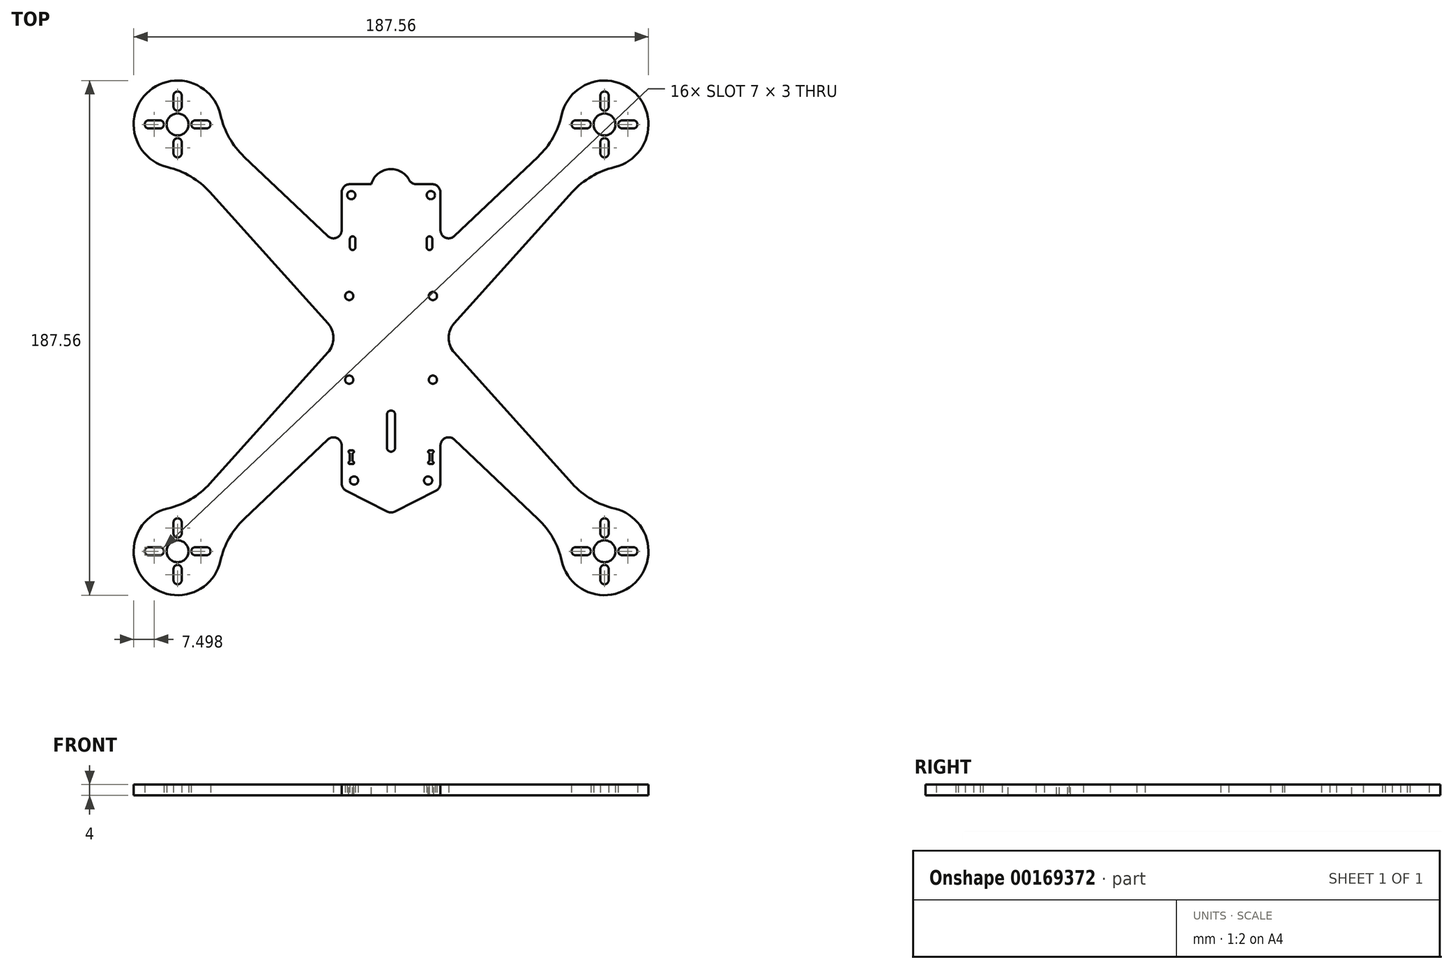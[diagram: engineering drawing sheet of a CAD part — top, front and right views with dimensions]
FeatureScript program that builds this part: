
annotation { "Feature Type Name" : "Feature", "Feature Type Description" : "" }
export const myFeature = defineFeature(function(context is Context, id is Id, definition is map)
    precondition{}
    {
        {
            var Q0;
            Q0=qCreatedBy(makeId("Top.planeOp"),FACE);
            var sketch = newSketch(context, id + "F0", { "sketchPlane" : qUnion([Q0])});
            skLineSegment(sketch, "E0.bottom", {"start": v(-15, 56) * mm, "end": v(15, 56) * mm});
            skLineSegment(sketch, "E0.left", {"start": v(-18, 53) * mm, "end": v(-18, 39.26) * mm});
            skLineSegment(sketch, "E0.right", {"start": v(18, 53) * mm, "end": v(18, 39.26) * mm});
            skCircle(sketch, "E1", {"center": v(0, 0) * mm, "radius": 110 * mm, "construction": true});
            skLineSegment(sketch, "E2", {"start": v(0, 0) * mm, "end": v(-77.78, 77.78) * mm, "construction": true});
            skLineSegment(sketch, "E3", {"start": v(0, 0) * mm, "end": v(-77.78, -77.78) * mm, "construction": true});
            skLineSegment(sketch, "E4", {"start": v(0, 0) * mm, "end": v(77.78, 77.78) * mm, "construction": true});
            skLineSegment(sketch, "E5", {"start": v(0, 0) * mm, "end": v(77.78, -77.78) * mm, "construction": true});
            skCircle(sketch, "E6", {"center": v(-77.78, 77.78) * mm, "radius": 63.5 * mm, "construction": true});
            skCircle(sketch, "E7", {"center": v(-77.78, -77.78) * mm, "radius": 63.5 * mm, "construction": true});
            skCircle(sketch, "E8", {"center": v(77.78, -77.78) * mm, "radius": 63.5 * mm, "construction": true});
            skCircle(sketch, "E9", {"center": v(77.78, 77.78) * mm, "radius": 63.5 * mm, "construction": true});
            skLineSegment(sketch, "E10.trimOffspring", {"start": v(-18, -39.26) * mm, "end": v(-18, -53) * mm});
            skLineSegment(sketch, "E11.trimOffspring", {"start": v(18, -39.26) * mm, "end": v(18, -53) * mm});
            skCircle(sketch, "E12", {"center": v(-15.25, 15.25) * mm, "radius": 1.5 * mm});
            skCircle(sketch, "E13.0.1.0", {"center": v(-15.25, -15.25) * mm, "radius": 1.5 * mm});
            skCircle(sketch, "E13.1.0.0", {"center": v(15.25, 15.25) * mm, "radius": 1.5 * mm});
            skCircle(sketch, "E13.1.1.0", {"center": v(15.25, -15.25) * mm, "radius": 1.5 * mm});
            skLineSegment(sketch, "E13.direction1", {"start": v(-15.25, 15.25) * mm, "end": v(15.25, 15.25) * mm, "construction": true});
            skLineSegment(sketch, "E13.direction2", {"start": v(-15.25, 15.25) * mm, "end": v(-15.25, -15.25) * mm, "construction": true});
            skPoint(sketch, "E14.visualSharp", {"position": v(-18, -32.28) * mm});
            skPoint(sketch, "E15.visualSharp", {"position": v(18, -32.28) * mm});
            skPoint(sketch, "E16.visualSharp", {"position": v(18, 32.28) * mm});
            skPoint(sketch, "E17.visualSharp", {"position": v(-18, 32.28) * mm});
            skCircle(sketch, "E18", {"center": v(-13.5, -52) * mm, "radius": 1.5 * mm});
            skCircle(sketch, "E19", {"center": v(-14.5, 52) * mm, "radius": 1.5 * mm});
            skCircle(sketch, "E20.1.0.0", {"center": v(14.5, 52) * mm, "radius": 1.5 * mm});
            skLineSegment(sketch, "E21", {"start": v(-14.5, 52) * mm, "end": v(14.5, 52) * mm, "construction": true});
            skCircle(sketch, "E22.1.0.0", {"center": v(13.5, -52) * mm, "radius": 1.5 * mm});
            skLineSegment(sketch, "E22.direction1", {"start": v(-13.5, -52) * mm, "end": v(13.5, -52) * mm, "construction": true});
            skPoint(sketch, "E23.visualSharp", {"position": v(-18, 56) * mm});
            skArc(sketch, "E23.filletArc", {"start": v(-15, 56) * mm, "mid": v(-17.12, 55.12) * mm, "end": v(-18, 53) * mm});
            skPoint(sketch, "E24.visualSharp", {"position": v(18, 56) * mm});
            skArc(sketch, "E24.filletArc", {"start": v(18, 53) * mm, "mid": v(17.12, 55.12) * mm, "end": v(15, 56) * mm});
            skArc(sketch, "E25", {"start": v(-81.44, -62.2) * mm, "mid": v(-89.03, -89.16) * mm, "end": v(-62.16, -81.25) * mm});
            skArc(sketch, "E26", {"start": v(62.16, -81.25) * mm, "mid": v(89.03, -89.16) * mm, "end": v(81.44, -62.2) * mm});
            skArc(sketch, "E27", {"start": v(81.44, 62.2) * mm, "mid": v(89.03, 89.16) * mm, "end": v(62.16, 81.25) * mm});
            skArc(sketch, "E28", {"start": v(-62.16, 81.25) * mm, "mid": v(-89.03, 89.16) * mm, "end": v(-81.44, 62.2) * mm});
            skLineSegment(sketch, "E29", {"start": v(-23.03, 5.35) * mm, "end": v(-66, 53.07) * mm});
            skLineSegment(sketch, "E30", {"start": v(-23.07, 37.08) * mm, "end": v(-53.53, 65.99) * mm});
            skPoint(sketch, "E31.visualSharp", {"position": v(-62.19, 74.2) * mm});
            skArc(sketch, "E31.filletArc", {"start": v(-62.16, 81.25) * mm, "mid": v(-58.98, 72.97) * mm, "end": v(-53.53, 65.99) * mm});
            skPoint(sketch, "E32.visualSharp", {"position": v(-74.2, 62.19) * mm});
            skArc(sketch, "E32.filletArc", {"start": v(-66, 53.07) * mm, "mid": v(-73.02, 58.82) * mm, "end": v(-81.44, 62.2) * mm});
            skLineSegment(sketch, "E33", {"start": v(23.07, 37.08) * mm, "end": v(53.53, 65.99) * mm});
            skLineSegment(sketch, "E34", {"start": v(23.03, 5.35) * mm, "end": v(66, 53.07) * mm});
            skPoint(sketch, "E35.visualSharp", {"position": v(62.19, 74.2) * mm});
            skArc(sketch, "E35.filletArc", {"start": v(53.53, 65.99) * mm, "mid": v(58.98, 72.97) * mm, "end": v(62.16, 81.25) * mm});
            skPoint(sketch, "E36.visualSharp", {"position": v(74.2, 62.19) * mm});
            skArc(sketch, "E36.filletArc", {"start": v(81.44, 62.2) * mm, "mid": v(73.02, 58.82) * mm, "end": v(66, 53.07) * mm});
            skLineSegment(sketch, "E37", {"start": v(-23.03, -5.35) * mm, "end": v(-66, -53.07) * mm});
            skLineSegment(sketch, "E38", {"start": v(-53.53, -65.99) * mm, "end": v(-23.07, -37.08) * mm});
            skLineSegment(sketch, "E39", {"start": v(23.07, -37.08) * mm, "end": v(53.53, -65.99) * mm});
            skLineSegment(sketch, "E40", {"start": v(66, -53.07) * mm, "end": v(23.03, -5.35) * mm});
            skPoint(sketch, "E41.visualSharp", {"position": v(-74.2, -62.19) * mm});
            skArc(sketch, "E41.filletArc", {"start": v(-81.44, -62.2) * mm, "mid": v(-73.02, -58.82) * mm, "end": v(-66, -53.07) * mm});
            skPoint(sketch, "E42.visualSharp", {"position": v(-62.19, -74.2) * mm});
            skArc(sketch, "E42.filletArc", {"start": v(-53.53, -65.99) * mm, "mid": v(-58.98, -72.97) * mm, "end": v(-62.16, -81.25) * mm});
            skPoint(sketch, "E43.visualSharp", {"position": v(62.19, -74.2) * mm});
            skArc(sketch, "E43.filletArc", {"start": v(62.16, -81.25) * mm, "mid": v(58.98, -72.97) * mm, "end": v(53.53, -65.99) * mm});
            skPoint(sketch, "E44.visualSharp", {"position": v(74.2, -62.19) * mm});
            skArc(sketch, "E44.filletArc", {"start": v(66, -53.07) * mm, "mid": v(73.02, -58.82) * mm, "end": v(81.44, -62.2) * mm});
            skCircle(sketch, "E45", {"center": v(-77.78, 77.78) * mm, "radius": 4 * mm});
            skCircle(sketch, "E46", {"center": v(77.78, 77.78) * mm, "radius": 4 * mm});
            skCircle(sketch, "E47", {"center": v(77.78, -77.78) * mm, "radius": 4 * mm});
            skCircle(sketch, "E48", {"center": v(-77.78, -77.78) * mm, "radius": 4 * mm});
            skArc(sketch, "E49", {"start": v(1.5, -28) * mm, "mid": v(0, -26.5) * mm, "end": v(-1.5, -28) * mm});
            skArc(sketch, "E50", {"start": v(-1.5, -40) * mm, "mid": v(0, -41.5) * mm, "end": v(1.5, -40) * mm});
            skLineSegment(sketch, "E51", {"start": v(-1.5, -28) * mm, "end": v(-1.5, -40) * mm});
            skLineSegment(sketch, "E52", {"start": v(1.5, -28) * mm, "end": v(1.5, -40) * mm});
            skArc(sketch, "E53.filletArc", {"start": v(-18, -39.26) * mm, "mid": v(-19.82, -36.5) * mm, "end": v(-23.07, -37.08) * mm});
            skArc(sketch, "E54.filletArc", {"start": v(23.07, -37.08) * mm, "mid": v(19.82, -36.5) * mm, "end": v(18, -39.26) * mm});
            skArc(sketch, "E55.filletArc", {"start": v(-23.07, 37.08) * mm, "mid": v(-19.82, 36.5) * mm, "end": v(-18, 39.26) * mm});
            skArc(sketch, "E56.filletArc", {"start": v(18, 39.26) * mm, "mid": v(19.82, 36.5) * mm, "end": v(23.07, 37.08) * mm});
            skArc(sketch, "E57", {"start": v(-13, 36) * mm, "mid": v(-14, 37) * mm, "end": v(-15, 36) * mm});
            skArc(sketch, "E58", {"start": v(-15, 33) * mm, "mid": v(-14, 32) * mm, "end": v(-13, 33) * mm});
            skLineSegment(sketch, "E59", {"start": v(-14, 36) * mm, "end": v(-14, 33) * mm, "construction": true});
            skLineSegment(sketch, "E60", {"start": v(-15, 36) * mm, "end": v(-15, 33) * mm});
            skLineSegment(sketch, "E61", {"start": v(-13, 36) * mm, "end": v(-13, 33) * mm});
            skLineSegment(sketch, "E62.MirrorCS", {"start": v(14, 36) * mm, "end": v(14, 33) * mm, "construction": true});
            skArc(sketch, "E63.MirrorCS", {"start": v(13, 36) * mm, "mid": v(14, 37) * mm, "end": v(15, 36) * mm});
            skArc(sketch, "E64.MirrorCS", {"start": v(15, 33) * mm, "mid": v(14, 32) * mm, "end": v(13, 33) * mm});
            skLineSegment(sketch, "E65.MirrorCS", {"start": v(13, 36) * mm, "end": v(13, 33) * mm});
            skLineSegment(sketch, "E66.MirrorCS", {"start": v(15, 36) * mm, "end": v(15, 33) * mm});
            skArc(sketch, "E67.filletArc", {"start": v(-23.03, -5.35) * mm, "mid": v(-20.98, 0) * mm, "end": v(-23.03, 5.35) * mm});
            skArc(sketch, "E68.filletArc", {"start": v(23.03, 5.35) * mm, "mid": v(20.98, 0) * mm, "end": v(23.03, -5.35) * mm});
            skLineSegment(sketch, "E69", {"start": v(-15, -56) * mm, "end": v(15, -56) * mm});
            skPoint(sketch, "E70.visualSharp", {"position": v(-18, -56) * mm});
            skArc(sketch, "E70.filletArc", {"start": v(-18, -53) * mm, "mid": v(-17.12, -55.12) * mm, "end": v(-15, -56) * mm});
            skPoint(sketch, "E71.visualSharp", {"position": v(18, -56) * mm});
            skArc(sketch, "E71.filletArc", {"start": v(15, -56) * mm, "mid": v(17.12, -55.12) * mm, "end": v(18, -53) * mm});
            skLineSegment(sketch, "E72", {"start": v(-77.78, 77.78) * mm, "end": v(-89.03, 89.16) * mm, "construction": true});
            skLineSegment(sketch, "E73", {"start": v(-77.78, 77.78) * mm, "end": v(-89.1, 66.47) * mm, "construction": true});
            skLineSegment(sketch, "E74", {"start": v(-77.78, 77.78) * mm, "end": v(-66.47, 89.1) * mm, "construction": true});
            skArc(sketch, "E75", {"start": v(-79.28, 84.28) * mm, "mid": v(-77.78, 82.78) * mm, "end": v(-76.28, 84.28) * mm});
            skArc(sketch, "E76", {"start": v(-76.28, 88.28) * mm, "mid": v(-77.78, 89.78) * mm, "end": v(-79.28, 88.28) * mm});
            skLineSegment(sketch, "E77", {"start": v(-79.28, 88.28) * mm, "end": v(-79.28, 84.28) * mm});
            skLineSegment(sketch, "E78", {"start": v(-76.28, 88.28) * mm, "end": v(-76.28, 84.28) * mm});
            skLineSegment(sketch, "E79", {"start": v(-77.78, 77.78) * mm, "end": v(-77.78, 93.78) * mm, "construction": true});
            skArc(sketch, "E80.1.0", {"start": v(-88.28, 79.28) * mm, "mid": v(-89.78, 77.78) * mm, "end": v(-88.28, 76.28) * mm});
            skArc(sketch, "E80.1.1", {"start": v(-84.28, 76.28) * mm, "mid": v(-82.78, 77.78) * mm, "end": v(-84.28, 79.28) * mm});
            skLineSegment(sketch, "E80.1.2", {"start": v(-88.28, 79.28) * mm, "end": v(-84.28, 79.28) * mm});
            skLineSegment(sketch, "E80.1.3", {"start": v(-88.28, 76.28) * mm, "end": v(-84.28, 76.28) * mm});
            skArc(sketch, "E80.2.0", {"start": v(-79.28, 67.28) * mm, "mid": v(-77.78, 65.78) * mm, "end": v(-76.28, 67.28) * mm});
            skArc(sketch, "E80.2.1", {"start": v(-76.28, 71.28) * mm, "mid": v(-77.78, 72.78) * mm, "end": v(-79.28, 71.28) * mm});
            skLineSegment(sketch, "E80.2.2", {"start": v(-79.28, 67.28) * mm, "end": v(-79.28, 71.28) * mm});
            skLineSegment(sketch, "E80.2.3", {"start": v(-76.28, 67.28) * mm, "end": v(-76.28, 71.28) * mm});
            skArc(sketch, "E80.3.0", {"start": v(-67.28, 76.28) * mm, "mid": v(-65.78, 77.78) * mm, "end": v(-67.28, 79.28) * mm});
            skArc(sketch, "E80.3.1", {"start": v(-71.28, 79.28) * mm, "mid": v(-72.78, 77.78) * mm, "end": v(-71.28, 76.28) * mm});
            skLineSegment(sketch, "E80.3.2", {"start": v(-67.28, 76.28) * mm, "end": v(-71.28, 76.28) * mm});
            skLineSegment(sketch, "E80.3.3", {"start": v(-67.28, 79.28) * mm, "end": v(-71.28, 79.28) * mm});
            skLineSegment(sketch, "E81.1.0", {"start": v(-88.28, -79.28) * mm, "end": v(-84.28, -79.28) * mm});
            skArc(sketch, "E81.1.1", {"start": v(-88.28, -76.28) * mm, "mid": v(-89.78, -77.78) * mm, "end": v(-88.28, -79.28) * mm});
            skLineSegment(sketch, "E81.1.2", {"start": v(-88.28, -76.28) * mm, "end": v(-84.28, -76.28) * mm});
            skArc(sketch, "E81.1.3", {"start": v(-84.28, -79.28) * mm, "mid": v(-82.78, -77.78) * mm, "end": v(-84.28, -76.28) * mm});
            skArc(sketch, "E81.1.4", {"start": v(-76.28, -67.28) * mm, "mid": v(-77.78, -65.78) * mm, "end": v(-79.28, -67.28) * mm});
            skLineSegment(sketch, "E81.1.5", {"start": v(-79.28, -67.28) * mm, "end": v(-79.28, -71.28) * mm});
            skLineSegment(sketch, "E81.1.6", {"start": v(-76.28, -67.28) * mm, "end": v(-76.28, -71.28) * mm});
            skArc(sketch, "E81.1.7", {"start": v(-79.28, -71.28) * mm, "mid": v(-77.78, -72.78) * mm, "end": v(-76.28, -71.28) * mm});
            skLineSegment(sketch, "E81.1.8", {"start": v(-67.28, -79.28) * mm, "end": v(-71.28, -79.28) * mm});
            skArc(sketch, "E81.1.9", {"start": v(-71.28, -76.28) * mm, "mid": v(-72.78, -77.78) * mm, "end": v(-71.28, -79.28) * mm});
            skLineSegment(sketch, "E81.1.10", {"start": v(-67.28, -76.28) * mm, "end": v(-71.28, -76.28) * mm});
            skArc(sketch, "E81.1.11", {"start": v(-67.28, -79.28) * mm, "mid": v(-65.78, -77.78) * mm, "end": v(-67.28, -76.28) * mm});
            skArc(sketch, "E81.1.12", {"start": v(-76.28, -84.28) * mm, "mid": v(-77.78, -82.78) * mm, "end": v(-79.28, -84.28) * mm});
            skLineSegment(sketch, "E81.1.13", {"start": v(-76.28, -88.28) * mm, "end": v(-76.28, -84.28) * mm});
            skLineSegment(sketch, "E81.1.14", {"start": v(-79.28, -88.28) * mm, "end": v(-79.28, -84.28) * mm});
            skArc(sketch, "E81.1.15", {"start": v(-79.28, -88.28) * mm, "mid": v(-77.78, -89.78) * mm, "end": v(-76.28, -88.28) * mm});
            skLineSegment(sketch, "E81.2.0", {"start": v(79.28, -88.28) * mm, "end": v(79.28, -84.28) * mm});
            skArc(sketch, "E81.2.1", {"start": v(76.28, -88.28) * mm, "mid": v(77.78, -89.78) * mm, "end": v(79.28, -88.28) * mm});
            skLineSegment(sketch, "E81.2.2", {"start": v(76.28, -88.28) * mm, "end": v(76.28, -84.28) * mm});
            skArc(sketch, "E81.2.3", {"start": v(79.28, -84.28) * mm, "mid": v(77.78, -82.78) * mm, "end": v(76.28, -84.28) * mm});
            skArc(sketch, "E81.2.4", {"start": v(67.28, -76.28) * mm, "mid": v(65.78, -77.78) * mm, "end": v(67.28, -79.28) * mm});
            skLineSegment(sketch, "E81.2.5", {"start": v(67.28, -79.28) * mm, "end": v(71.28, -79.28) * mm});
            skLineSegment(sketch, "E81.2.6", {"start": v(67.28, -76.28) * mm, "end": v(71.28, -76.28) * mm});
            skArc(sketch, "E81.2.7", {"start": v(71.28, -79.28) * mm, "mid": v(72.78, -77.78) * mm, "end": v(71.28, -76.28) * mm});
            skLineSegment(sketch, "E81.2.8", {"start": v(79.28, -67.28) * mm, "end": v(79.28, -71.28) * mm});
            skArc(sketch, "E81.2.9", {"start": v(76.28, -71.28) * mm, "mid": v(77.78, -72.78) * mm, "end": v(79.28, -71.28) * mm});
            skLineSegment(sketch, "E81.2.10", {"start": v(76.28, -67.28) * mm, "end": v(76.28, -71.28) * mm});
            skArc(sketch, "E81.2.11", {"start": v(79.28, -67.28) * mm, "mid": v(77.78, -65.78) * mm, "end": v(76.28, -67.28) * mm});
            skArc(sketch, "E81.2.12", {"start": v(84.28, -76.28) * mm, "mid": v(82.78, -77.78) * mm, "end": v(84.28, -79.28) * mm});
            skLineSegment(sketch, "E81.2.13", {"start": v(88.28, -76.28) * mm, "end": v(84.28, -76.28) * mm});
            skLineSegment(sketch, "E81.2.14", {"start": v(88.28, -79.28) * mm, "end": v(84.28, -79.28) * mm});
            skArc(sketch, "E81.2.15", {"start": v(88.28, -79.28) * mm, "mid": v(89.78, -77.78) * mm, "end": v(88.28, -76.28) * mm});
            skLineSegment(sketch, "E81.3.0", {"start": v(88.28, 79.28) * mm, "end": v(84.28, 79.28) * mm});
            skArc(sketch, "E81.3.1", {"start": v(88.28, 76.28) * mm, "mid": v(89.78, 77.78) * mm, "end": v(88.28, 79.28) * mm});
            skLineSegment(sketch, "E81.3.2", {"start": v(88.28, 76.28) * mm, "end": v(84.28, 76.28) * mm});
            skArc(sketch, "E81.3.3", {"start": v(84.28, 79.28) * mm, "mid": v(82.78, 77.78) * mm, "end": v(84.28, 76.28) * mm});
            skArc(sketch, "E81.3.4", {"start": v(76.28, 67.28) * mm, "mid": v(77.78, 65.78) * mm, "end": v(79.28, 67.28) * mm});
            skLineSegment(sketch, "E81.3.5", {"start": v(79.28, 67.28) * mm, "end": v(79.28, 71.28) * mm});
            skLineSegment(sketch, "E81.3.6", {"start": v(76.28, 67.28) * mm, "end": v(76.28, 71.28) * mm});
            skArc(sketch, "E81.3.7", {"start": v(79.28, 71.28) * mm, "mid": v(77.78, 72.78) * mm, "end": v(76.28, 71.28) * mm});
            skLineSegment(sketch, "E81.3.8", {"start": v(67.28, 79.28) * mm, "end": v(71.28, 79.28) * mm});
            skArc(sketch, "E81.3.9", {"start": v(71.28, 76.28) * mm, "mid": v(72.78, 77.78) * mm, "end": v(71.28, 79.28) * mm});
            skLineSegment(sketch, "E81.3.10", {"start": v(67.28, 76.28) * mm, "end": v(71.28, 76.28) * mm});
            skArc(sketch, "E81.3.11", {"start": v(67.28, 79.28) * mm, "mid": v(65.78, 77.78) * mm, "end": v(67.28, 76.28) * mm});
            skArc(sketch, "E81.3.12", {"start": v(76.28, 84.28) * mm, "mid": v(77.78, 82.78) * mm, "end": v(79.28, 84.28) * mm});
            skLineSegment(sketch, "E81.3.13", {"start": v(76.28, 88.28) * mm, "end": v(76.28, 84.28) * mm});
            skLineSegment(sketch, "E81.3.14", {"start": v(79.28, 88.28) * mm, "end": v(79.28, 84.28) * mm});
            skArc(sketch, "E81.3.15", {"start": v(79.28, 88.28) * mm, "mid": v(77.78, 89.78) * mm, "end": v(76.28, 88.28) * mm});
            skLineSegment(sketch, "E82", {"start": v(-93.78, -77.78) * mm, "end": v(-61.17, -77.78) * mm, "construction": true});
            skLineSegment(sketch, "E83", {"start": v(-77.78, -93.78) * mm, "end": v(-77.78, -61.1) * mm, "construction": true});
            skPoint(sketch, "E83.endSnap0", {"position": v(-77.78, -65.78) * mm});
            skSolve(sketch);
        }
        {
            var Q0;
            Q0 = qSketchRegion(id + "F0", true);
            extrude(context, id + "F1", {"entities" : qUnion([Q0]), "depth" : 4 * mm});
        }
        {
            var Q0;
            Q0=makeQuery(id+"F1.opExtrude","CAP_FACE",FACE,{"disambiguationData":[OSD([sQuery(id+"F0.wireOp",EDGE,"E0.bottom"),sQuery(id+"F0.wireOp",EDGE,"E0.left"),sQuery(id+"F0.wireOp",EDGE,"E0.right"),sQuery(id+"F0.wireOp",EDGE,"E10.trimOffspring"),sQuery(id+"F0.wireOp",EDGE,"E11.trimOffspring"),sQuery(id+"F0.wireOp",EDGE,"E12"),sQuery(id+"F0.wireOp",EDGE,"E13.0.1.0"),sQuery(id+"F0.wireOp",EDGE,"E13.1.0.0"),sQuery(id+"F0.wireOp",EDGE,"E13.1.1.0"),sQuery(id+"F0.wireOp",EDGE,"E18"),sQuery(id+"F0.wireOp",EDGE,"E19"),sQuery(id+"F0.wireOp",EDGE,"E20.1.0.0"),sQuery(id+"F0.wireOp",EDGE,"E22.1.0.0"),sQuery(id+"F0.wireOp",EDGE,"E23.filletArc"),sQuery(id+"F0.wireOp",EDGE,"E24.filletArc"),sQuery(id+"F0.wireOp",EDGE,"E25"),sQuery(id+"F0.wireOp",EDGE,"E26"),sQuery(id+"F0.wireOp",EDGE,"E27"),sQuery(id+"F0.wireOp",EDGE,"E28"),sQuery(id+"F0.wireOp",EDGE,"E29"),sQuery(id+"F0.wireOp",EDGE,"E30"),sQuery(id+"F0.wireOp",EDGE,"E31.filletArc"),sQuery(id+"F0.wireOp",EDGE,"E32.filletArc"),sQuery(id+"F0.wireOp",EDGE,"E33"),sQuery(id+"F0.wireOp",EDGE,"E34"),sQuery(id+"F0.wireOp",EDGE,"E35.filletArc"),sQuery(id+"F0.wireOp",EDGE,"E36.filletArc"),sQuery(id+"F0.wireOp",EDGE,"E37"),sQuery(id+"F0.wireOp",EDGE,"E38"),sQuery(id+"F0.wireOp",EDGE,"E39"),sQuery(id+"F0.wireOp",EDGE,"E40"),sQuery(id+"F0.wireOp",EDGE,"E41.filletArc"),sQuery(id+"F0.wireOp",EDGE,"E42.filletArc"),sQuery(id+"F0.wireOp",EDGE,"E43.filletArc"),sQuery(id+"F0.wireOp",EDGE,"E44.filletArc"),sQuery(id+"F0.wireOp",EDGE,"E45"),sQuery(id+"F0.wireOp",EDGE,"E46"),sQuery(id+"F0.wireOp",EDGE,"E47"),sQuery(id+"F0.wireOp",EDGE,"E48"),sQuery(id+"F0.wireOp",EDGE,"E49"),sQuery(id+"F0.wireOp",EDGE,"E50"),sQuery(id+"F0.wireOp",EDGE,"E51"),sQuery(id+"F0.wireOp",EDGE,"E52"),sQuery(id+"F0.wireOp",EDGE,"E53.filletArc"),sQuery(id+"F0.wireOp",EDGE,"E54.filletArc"),sQuery(id+"F0.wireOp",EDGE,"E55.filletArc"),sQuery(id+"F0.wireOp",EDGE,"E56.filletArc"),sQuery(id+"F0.wireOp",EDGE,"E57"),sQuery(id+"F0.wireOp",EDGE,"E58"),sQuery(id+"F0.wireOp",EDGE,"E60"),sQuery(id+"F0.wireOp",EDGE,"E61"),sQuery(id+"F0.wireOp",EDGE,"E63.MirrorCS"),sQuery(id+"F0.wireOp",EDGE,"E64.MirrorCS"),sQuery(id+"F0.wireOp",EDGE,"E65.MirrorCS"),sQuery(id+"F0.wireOp",EDGE,"E66.MirrorCS"),sQuery(id+"F0.wireOp",EDGE,"E67.filletArc"),sQuery(id+"F0.wireOp",EDGE,"E68.filletArc"),sQuery(id+"F0.wireOp",EDGE,"OCQb3uI1-uvxJ-f9Up-c4JK-0uccdhJYX1hB.left"),sQuery(id+"F0.wireOp",EDGE,"OCQb3uI1-uvxJ-f9Up-c4JK-0uccdhJYX1hB.right"),sQuery(id+"F0.wireOp",EDGE,"yTLhHzRo-9fRE-Ol12-0E4a-2OdcbhfDfOt4"),sQuery(id+"F0.wireOp",EDGE,"H9Q5S8l5-goRD-GTd5-hdNk-WrsdtsOP4wSm"),sQuery(id+"F0.wireOp",EDGE,"62a1f2fa-edf9-4163-9542-a3ea3378514f0.MirrorCS"),sQuery(id+"F0.wireOp",EDGE,"62a1f2fa-edf9-4163-9542-a3ea3378514f1.MirrorCS"),sQuery(id+"F0.wireOp",EDGE,"62a1f2fa-edf9-4163-9542-a3ea3378514f2.MirrorCS"),sQuery(id+"F0.wireOp",EDGE,"62a1f2fa-edf9-4163-9542-a3ea3378514f4.MirrorCS"),sQuery(id+"F0.wireOp",EDGE,"E69"),sQuery(id+"F0.wireOp",EDGE,"E70.filletArc"),sQuery(id+"F0.wireOp",EDGE,"E71.filletArc"),sQuery(id+"F0.wireOp",EDGE,"E75"),sQuery(id+"F0.wireOp",EDGE,"E76"),sQuery(id+"F0.wireOp",EDGE,"E77"),sQuery(id+"F0.wireOp",EDGE,"E78"),sQuery(id+"F0.wireOp",EDGE,"E80.1.0"),sQuery(id+"F0.wireOp",EDGE,"E80.1.1"),sQuery(id+"F0.wireOp",EDGE,"E80.1.2"),sQuery(id+"F0.wireOp",EDGE,"E80.1.3"),sQuery(id+"F0.wireOp",EDGE,"E80.2.0"),sQuery(id+"F0.wireOp",EDGE,"E80.2.1"),sQuery(id+"F0.wireOp",EDGE,"E80.2.2"),sQuery(id+"F0.wireOp",EDGE,"E80.2.3"),sQuery(id+"F0.wireOp",EDGE,"E80.3.0"),sQuery(id+"F0.wireOp",EDGE,"E80.3.1"),sQuery(id+"F0.wireOp",EDGE,"E80.3.2"),sQuery(id+"F0.wireOp",EDGE,"E80.3.3"),sQuery(id+"F0.wireOp",EDGE,"E81.1.0"),sQuery(id+"F0.wireOp",EDGE,"E81.1.1"),sQuery(id+"F0.wireOp",EDGE,"E81.1.2"),sQuery(id+"F0.wireOp",EDGE,"E81.1.3"),sQuery(id+"F0.wireOp",EDGE,"E81.1.4"),sQuery(id+"F0.wireOp",EDGE,"E81.1.5"),sQuery(id+"F0.wireOp",EDGE,"E81.1.6"),sQuery(id+"F0.wireOp",EDGE,"E81.1.7"),sQuery(id+"F0.wireOp",EDGE,"E81.1.8"),sQuery(id+"F0.wireOp",EDGE,"E81.1.9"),sQuery(id+"F0.wireOp",EDGE,"E81.1.10"),sQuery(id+"F0.wireOp",EDGE,"E81.1.11"),sQuery(id+"F0.wireOp",EDGE,"E81.1.12"),sQuery(id+"F0.wireOp",EDGE,"E81.1.13"),sQuery(id+"F0.wireOp",EDGE,"E81.1.14"),sQuery(id+"F0.wireOp",EDGE,"E81.1.15"),sQuery(id+"F0.wireOp",EDGE,"E81.2.0"),sQuery(id+"F0.wireOp",EDGE,"E81.2.1"),sQuery(id+"F0.wireOp",EDGE,"E81.2.2"),sQuery(id+"F0.wireOp",EDGE,"E81.2.3"),sQuery(id+"F0.wireOp",EDGE,"E81.2.4"),sQuery(id+"F0.wireOp",EDGE,"E81.2.5"),sQuery(id+"F0.wireOp",EDGE,"E81.2.6"),sQuery(id+"F0.wireOp",EDGE,"E81.2.7"),sQuery(id+"F0.wireOp",EDGE,"E81.2.8"),sQuery(id+"F0.wireOp",EDGE,"E81.2.9"),sQuery(id+"F0.wireOp",EDGE,"E81.2.10"),sQuery(id+"F0.wireOp",EDGE,"E81.2.11"),sQuery(id+"F0.wireOp",EDGE,"E81.2.12"),sQuery(id+"F0.wireOp",EDGE,"E81.2.13"),sQuery(id+"F0.wireOp",EDGE,"E81.2.14"),sQuery(id+"F0.wireOp",EDGE,"E81.2.15"),sQuery(id+"F0.wireOp",EDGE,"E81.3.0"),sQuery(id+"F0.wireOp",EDGE,"E81.3.1"),sQuery(id+"F0.wireOp",EDGE,"E81.3.2"),sQuery(id+"F0.wireOp",EDGE,"E81.3.3"),sQuery(id+"F0.wireOp",EDGE,"E81.3.4"),sQuery(id+"F0.wireOp",EDGE,"E81.3.5"),sQuery(id+"F0.wireOp",EDGE,"E81.3.6"),sQuery(id+"F0.wireOp",EDGE,"E81.3.7"),sQuery(id+"F0.wireOp",EDGE,"E81.3.8"),sQuery(id+"F0.wireOp",EDGE,"E81.3.9"),sQuery(id+"F0.wireOp",EDGE,"E81.3.10"),sQuery(id+"F0.wireOp",EDGE,"E81.3.11"),sQuery(id+"F0.wireOp",EDGE,"E81.3.12"),sQuery(id+"F0.wireOp",EDGE,"E81.3.13"),sQuery(id+"F0.wireOp",EDGE,"E81.3.14"),sQuery(id+"F0.wireOp",EDGE,"E81.3.15")])],"isStart":false});
            var sketch = newSketch(context, id + "F2", { "sketchPlane" : qUnion([Q0])});
            skLineSegment(sketch, "E84.bottom", {"start": v(-15, -41) * mm, "end": v(-14, -41) * mm});
            skLineSegment(sketch, "E84.top", {"start": v(-15, -46) * mm, "end": v(-14, -46) * mm});
            skLineSegment(sketch, "E84.right", {"start": v(-14, -42) * mm, "end": v(-14, -45) * mm});
            skArc(sketch, "E85", {"start": v(-14, -46) * mm, "mid": v(-13.5, -45.5) * mm, "end": v(-14, -45) * mm});
            skArc(sketch, "E86", {"start": v(-15, -45) * mm, "mid": v(-15.5, -45.5) * mm, "end": v(-15, -46) * mm});
            skArc(sketch, "E87", {"start": v(-15, -41) * mm, "mid": v(-15.5, -41.5) * mm, "end": v(-15, -42) * mm});
            skArc(sketch, "E88", {"start": v(-14, -42) * mm, "mid": v(-13.5, -41.5) * mm, "end": v(-14, -41) * mm});
            skLineSegment(sketch, "E89.trimOffspring", {"start": v(-15, -42) * mm, "end": v(-15, -45) * mm});
            skArc(sketch, "E90.MirrorCS", {"start": v(15, -45) * mm, "mid": v(15.5, -45.5) * mm, "end": v(15, -46) * mm});
            skLineSegment(sketch, "E91.MirrorCS", {"start": v(15, -46) * mm, "end": v(14, -46) * mm});
            skLineSegment(sketch, "E92.MirrorCS", {"start": v(15, -41) * mm, "end": v(14, -41) * mm});
            skArc(sketch, "E93.MirrorCS", {"start": v(14, -46) * mm, "mid": v(13.5, -45.5) * mm, "end": v(14, -45) * mm});
            skArc(sketch, "E94.MirrorCS", {"start": v(14, -42) * mm, "mid": v(13.5, -41.5) * mm, "end": v(14, -41) * mm});
            skArc(sketch, "E95.MirrorCS", {"start": v(15, -41) * mm, "mid": v(15.5, -41.5) * mm, "end": v(15, -42) * mm});
            skLineSegment(sketch, "E96.MirrorCS", {"start": v(15, -42) * mm, "end": v(15, -45) * mm});
            skLineSegment(sketch, "E97.MirrorCS", {"start": v(14, -42) * mm, "end": v(14, -45) * mm});
            skSolve(sketch);
        }
        {
            var Q0;
            Q0 = qSketchRegion(id + "F2", true);
            extrude(context, id + "F3", {"entities" : qUnion([Q0]), "operationType" : NewBodyOperationType.REMOVE, "endBound" : BoundingType.THROUGH_ALL, "oppositeDirection" : true, "depth" : 25 * mm});
        }
        {
            var Q0;
            Q0=makeQuery(id+"F1.opExtrude","CAP_FACE",FACE,{"disambiguationData":[OSD([sQuery(id+"F0.wireOp",EDGE,"E0.bottom"),sQuery(id+"F0.wireOp",EDGE,"E0.left"),sQuery(id+"F0.wireOp",EDGE,"E0.right"),sQuery(id+"F0.wireOp",EDGE,"E10.trimOffspring"),sQuery(id+"F0.wireOp",EDGE,"E11.trimOffspring"),sQuery(id+"F0.wireOp",EDGE,"E12"),sQuery(id+"F0.wireOp",EDGE,"E13.0.1.0"),sQuery(id+"F0.wireOp",EDGE,"E13.1.0.0"),sQuery(id+"F0.wireOp",EDGE,"E13.1.1.0"),sQuery(id+"F0.wireOp",EDGE,"E18"),sQuery(id+"F0.wireOp",EDGE,"E19"),sQuery(id+"F0.wireOp",EDGE,"E20.1.0.0"),sQuery(id+"F0.wireOp",EDGE,"E22.1.0.0"),sQuery(id+"F0.wireOp",EDGE,"E23.filletArc"),sQuery(id+"F0.wireOp",EDGE,"E24.filletArc"),sQuery(id+"F0.wireOp",EDGE,"E25"),sQuery(id+"F0.wireOp",EDGE,"E26"),sQuery(id+"F0.wireOp",EDGE,"E27"),sQuery(id+"F0.wireOp",EDGE,"E28"),sQuery(id+"F0.wireOp",EDGE,"E29"),sQuery(id+"F0.wireOp",EDGE,"E30"),sQuery(id+"F0.wireOp",EDGE,"E31.filletArc"),sQuery(id+"F0.wireOp",EDGE,"E32.filletArc"),sQuery(id+"F0.wireOp",EDGE,"E33"),sQuery(id+"F0.wireOp",EDGE,"E34"),sQuery(id+"F0.wireOp",EDGE,"E35.filletArc"),sQuery(id+"F0.wireOp",EDGE,"E36.filletArc"),sQuery(id+"F0.wireOp",EDGE,"E37"),sQuery(id+"F0.wireOp",EDGE,"E38"),sQuery(id+"F0.wireOp",EDGE,"E39"),sQuery(id+"F0.wireOp",EDGE,"E40"),sQuery(id+"F0.wireOp",EDGE,"E41.filletArc"),sQuery(id+"F0.wireOp",EDGE,"E42.filletArc"),sQuery(id+"F0.wireOp",EDGE,"E43.filletArc"),sQuery(id+"F0.wireOp",EDGE,"E44.filletArc"),sQuery(id+"F0.wireOp",EDGE,"E45"),sQuery(id+"F0.wireOp",EDGE,"E46"),sQuery(id+"F0.wireOp",EDGE,"E47"),sQuery(id+"F0.wireOp",EDGE,"E48"),sQuery(id+"F0.wireOp",EDGE,"E49"),sQuery(id+"F0.wireOp",EDGE,"E50"),sQuery(id+"F0.wireOp",EDGE,"E51"),sQuery(id+"F0.wireOp",EDGE,"E52"),sQuery(id+"F0.wireOp",EDGE,"E53.filletArc"),sQuery(id+"F0.wireOp",EDGE,"E54.filletArc"),sQuery(id+"F0.wireOp",EDGE,"E55.filletArc"),sQuery(id+"F0.wireOp",EDGE,"E56.filletArc"),sQuery(id+"F0.wireOp",EDGE,"E57"),sQuery(id+"F0.wireOp",EDGE,"E58"),sQuery(id+"F0.wireOp",EDGE,"E60"),sQuery(id+"F0.wireOp",EDGE,"E61"),sQuery(id+"F0.wireOp",EDGE,"E63.MirrorCS"),sQuery(id+"F0.wireOp",EDGE,"E64.MirrorCS"),sQuery(id+"F0.wireOp",EDGE,"E65.MirrorCS"),sQuery(id+"F0.wireOp",EDGE,"E66.MirrorCS"),sQuery(id+"F0.wireOp",EDGE,"E67.filletArc"),sQuery(id+"F0.wireOp",EDGE,"E68.filletArc"),sQuery(id+"F0.wireOp",EDGE,"OCQb3uI1-uvxJ-f9Up-c4JK-0uccdhJYX1hB.left"),sQuery(id+"F0.wireOp",EDGE,"OCQb3uI1-uvxJ-f9Up-c4JK-0uccdhJYX1hB.right"),sQuery(id+"F0.wireOp",EDGE,"yTLhHzRo-9fRE-Ol12-0E4a-2OdcbhfDfOt4"),sQuery(id+"F0.wireOp",EDGE,"H9Q5S8l5-goRD-GTd5-hdNk-WrsdtsOP4wSm"),sQuery(id+"F0.wireOp",EDGE,"62a1f2fa-edf9-4163-9542-a3ea3378514f0.MirrorCS"),sQuery(id+"F0.wireOp",EDGE,"62a1f2fa-edf9-4163-9542-a3ea3378514f1.MirrorCS"),sQuery(id+"F0.wireOp",EDGE,"62a1f2fa-edf9-4163-9542-a3ea3378514f2.MirrorCS"),sQuery(id+"F0.wireOp",EDGE,"62a1f2fa-edf9-4163-9542-a3ea3378514f4.MirrorCS"),sQuery(id+"F0.wireOp",EDGE,"E69"),sQuery(id+"F0.wireOp",EDGE,"E70.filletArc"),sQuery(id+"F0.wireOp",EDGE,"E71.filletArc"),sQuery(id+"F0.wireOp",EDGE,"E75"),sQuery(id+"F0.wireOp",EDGE,"E76"),sQuery(id+"F0.wireOp",EDGE,"E77"),sQuery(id+"F0.wireOp",EDGE,"E78"),sQuery(id+"F0.wireOp",EDGE,"E80.1.0"),sQuery(id+"F0.wireOp",EDGE,"E80.1.1"),sQuery(id+"F0.wireOp",EDGE,"E80.1.2"),sQuery(id+"F0.wireOp",EDGE,"E80.1.3"),sQuery(id+"F0.wireOp",EDGE,"E80.2.0"),sQuery(id+"F0.wireOp",EDGE,"E80.2.1"),sQuery(id+"F0.wireOp",EDGE,"E80.2.2"),sQuery(id+"F0.wireOp",EDGE,"E80.2.3"),sQuery(id+"F0.wireOp",EDGE,"E80.3.0"),sQuery(id+"F0.wireOp",EDGE,"E80.3.1"),sQuery(id+"F0.wireOp",EDGE,"E80.3.2"),sQuery(id+"F0.wireOp",EDGE,"E80.3.3"),sQuery(id+"F0.wireOp",EDGE,"E81.1.0"),sQuery(id+"F0.wireOp",EDGE,"E81.1.1"),sQuery(id+"F0.wireOp",EDGE,"E81.1.2"),sQuery(id+"F0.wireOp",EDGE,"E81.1.3"),sQuery(id+"F0.wireOp",EDGE,"E81.1.4"),sQuery(id+"F0.wireOp",EDGE,"E81.1.5"),sQuery(id+"F0.wireOp",EDGE,"E81.1.6"),sQuery(id+"F0.wireOp",EDGE,"E81.1.7"),sQuery(id+"F0.wireOp",EDGE,"E81.1.8"),sQuery(id+"F0.wireOp",EDGE,"E81.1.9"),sQuery(id+"F0.wireOp",EDGE,"E81.1.10"),sQuery(id+"F0.wireOp",EDGE,"E81.1.11"),sQuery(id+"F0.wireOp",EDGE,"E81.1.12"),sQuery(id+"F0.wireOp",EDGE,"E81.1.13"),sQuery(id+"F0.wireOp",EDGE,"E81.1.14"),sQuery(id+"F0.wireOp",EDGE,"E81.1.15"),sQuery(id+"F0.wireOp",EDGE,"E81.2.0"),sQuery(id+"F0.wireOp",EDGE,"E81.2.1"),sQuery(id+"F0.wireOp",EDGE,"E81.2.2"),sQuery(id+"F0.wireOp",EDGE,"E81.2.3"),sQuery(id+"F0.wireOp",EDGE,"E81.2.4"),sQuery(id+"F0.wireOp",EDGE,"E81.2.5"),sQuery(id+"F0.wireOp",EDGE,"E81.2.6"),sQuery(id+"F0.wireOp",EDGE,"E81.2.7"),sQuery(id+"F0.wireOp",EDGE,"E81.2.8"),sQuery(id+"F0.wireOp",EDGE,"E81.2.9"),sQuery(id+"F0.wireOp",EDGE,"E81.2.10"),sQuery(id+"F0.wireOp",EDGE,"E81.2.11"),sQuery(id+"F0.wireOp",EDGE,"E81.2.12"),sQuery(id+"F0.wireOp",EDGE,"E81.2.13"),sQuery(id+"F0.wireOp",EDGE,"E81.2.14"),sQuery(id+"F0.wireOp",EDGE,"E81.2.15"),sQuery(id+"F0.wireOp",EDGE,"E81.3.0"),sQuery(id+"F0.wireOp",EDGE,"E81.3.1"),sQuery(id+"F0.wireOp",EDGE,"E81.3.2"),sQuery(id+"F0.wireOp",EDGE,"E81.3.3"),sQuery(id+"F0.wireOp",EDGE,"E81.3.4"),sQuery(id+"F0.wireOp",EDGE,"E81.3.5"),sQuery(id+"F0.wireOp",EDGE,"E81.3.6"),sQuery(id+"F0.wireOp",EDGE,"E81.3.7"),sQuery(id+"F0.wireOp",EDGE,"E81.3.8"),sQuery(id+"F0.wireOp",EDGE,"E81.3.9"),sQuery(id+"F0.wireOp",EDGE,"E81.3.10"),sQuery(id+"F0.wireOp",EDGE,"E81.3.11"),sQuery(id+"F0.wireOp",EDGE,"E81.3.12"),sQuery(id+"F0.wireOp",EDGE,"E81.3.13"),sQuery(id+"F0.wireOp",EDGE,"E81.3.14"),sQuery(id+"F0.wireOp",EDGE,"E81.3.15")])],"isStart":false});
            var sketch = newSketch(context, id + "F4", { "sketchPlane" : qUnion([Q0])});
            skLineSegment(sketch, "E98", {"start": v(-16.36, -55.67) * mm, "end": v(-1.36, -63.3) * mm});
            skLineSegment(sketch, "E99", {"start": v(1.36, -63.3) * mm, "end": v(16.36, -55.67) * mm});
            skPoint(sketch, "E100.visualSharp", {"position": v(0, -64) * mm});
            skArc(sketch, "E100.filletArc", {"start": v(-1.36, -63.3) * mm, "mid": v(0, -63.63) * mm, "end": v(1.36, -63.3) * mm});
            skCircle(sketch, "E101", {"center": v(0, 54) * mm, "radius": 7.5 * mm});
            skSolve(sketch);
        }
        {
            var Q0;
            {var subQ2=sQuery(id+"F4.wireOp",EDGE,"E98");Q0=makeQuery(id+"F4.imprint","IMPRINT",FACE,{"disambiguationData":[TD([[makeQuery(id+"F4.imprint","IMPRINT",EDGE,{"derivedFrom":subQ2}),1.0]])]});}
            var Q1;
            {var subQ0=sQuery(id+"F4.wireOp",EDGE,"E101");var subQ1=makeQuery(id+"F1.opExtrude","CAP_EDGE",EDGE,{"disambiguationData":[OSD([sQuery(id+"F0.wireOp",EDGE,"E0.bottom")])],"isStart":false});var subQ2=makeQuery(id+"F4.imprint","INTERSECT",VERTEX,{"disambiguationData":[OD(0.0)],"derivedFrom":[subQ1,subQ0]});Q1=makeQuery(id+"F4.imprint","IMPRINT",FACE,{"disambiguationData":[TD([[makeQuery(id+"F4.imprint","IMPRINT",EDGE,{"disambiguationData":[TD([[subQ2,1.0]])],"derivedFrom":subQ0}),1.0]])]});}
            extrude(context, id + "F5", {"entities" : qUnion([Q0, Q1]), "operationType" : NewBodyOperationType.ADD, "oppositeDirection" : true, "depth" : 4 * mm});
        }
        {
            var Q0;
            {var subQ0=sQuery(id+"F4.wireOp",EDGE,"E101");var subQ1=sQuery(id+"F0.wireOp",EDGE,"E0.bottom");Q0=makeQuery(id+"F5.opExtrude","SWEPT_EDGE",EDGE,{"disambiguationData":[OSD([subQ1,subQ0]),TDD([makeQuery(id+"F4.imprint","INTERSECT",VERTEX,{"disambiguationData":[OD(0.0)],"derivedFrom":[makeQuery(id+"F1.opExtrude","CAP_EDGE",EDGE,{"disambiguationData":[OSD([subQ1])],"isStart":false}),subQ0]})])]});}
            var Q1;
            {var subQ0=sQuery(id+"F4.wireOp",EDGE,"E101");var subQ1=sQuery(id+"F0.wireOp",EDGE,"E0.bottom");Q1=makeQuery(id+"F5.opExtrude","SWEPT_EDGE",EDGE,{"disambiguationData":[OSD([subQ1,subQ0]),TDD([makeQuery(id+"F4.imprint","INTERSECT",VERTEX,{"disambiguationData":[OD(1.0)],"derivedFrom":[makeQuery(id+"F1.opExtrude","CAP_EDGE",EDGE,{"disambiguationData":[OSD([subQ1])],"isStart":false}),subQ0]})])]});}
            fillet(context, id + "F6", {"entities" : qUnion([Q0, Q1]), "radius" : 3 * mm, "tangentPropagation" : true, "allowEdgeOverflow" : false});
        }
    });
